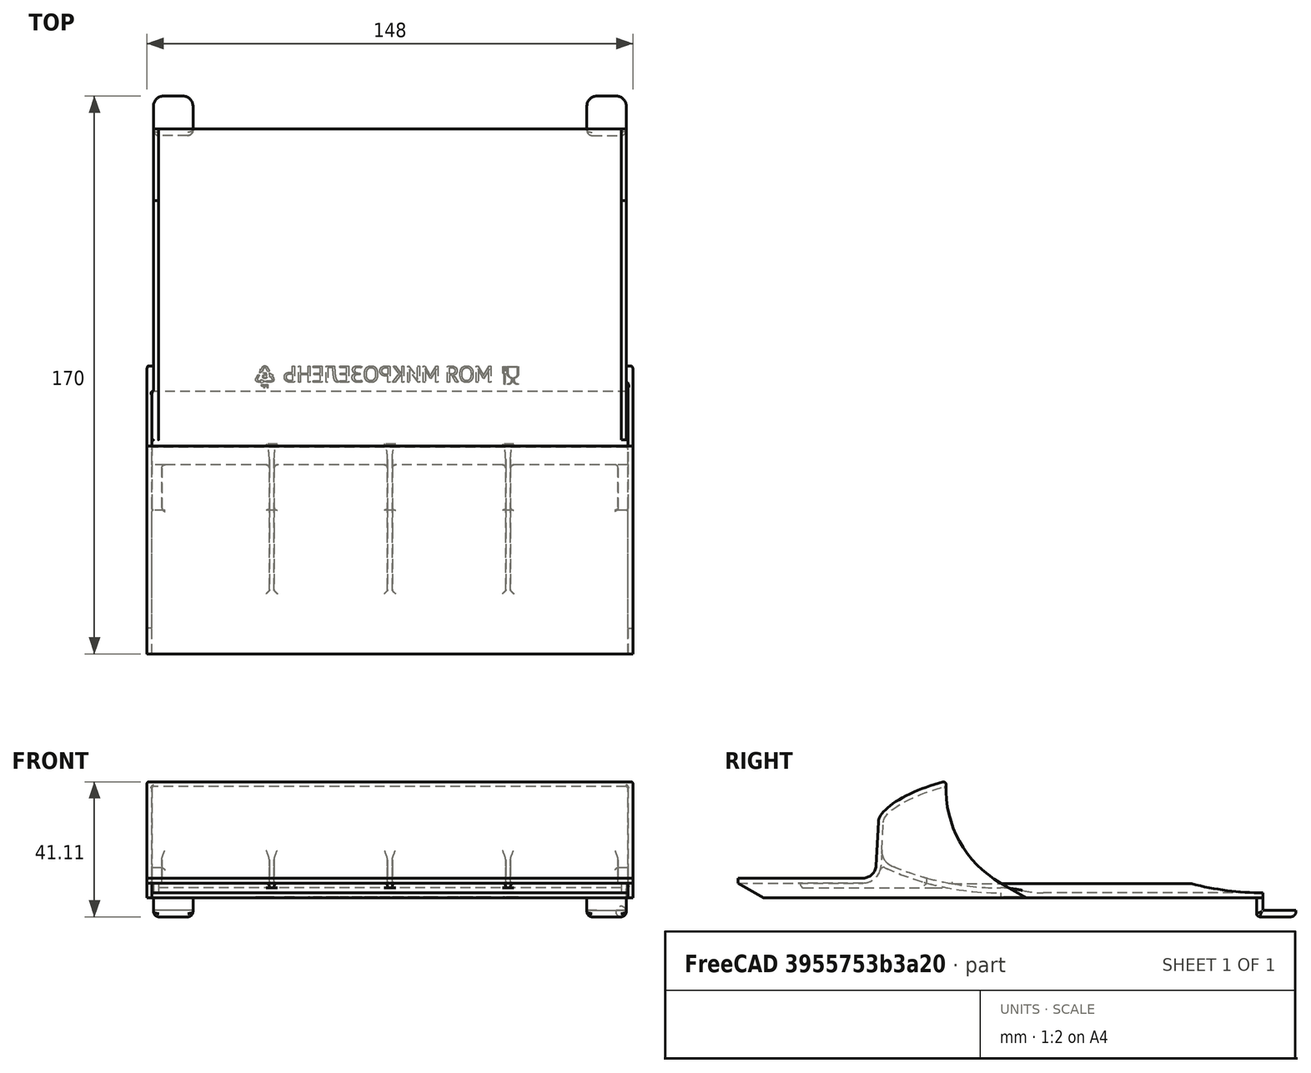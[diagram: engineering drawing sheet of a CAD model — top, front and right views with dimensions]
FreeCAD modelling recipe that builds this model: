
FCSTD DOCUMENT  (FreeCAD 1.1R38827 (Git))
Label: module
License: All rights reserved
LicenseURL: http://en.wikipedia.org/wiki/All_rights_reserved
objects: Sketcher::SketchObject×2, Part::Feature×1, PartDesign::FeatureBase×1, PartDesign::Body×1, Spreadsheet::Sheet×1
note: 8 computed .brp shape members not serialized (recipe doc carries the construction recipe); baked Part::Feature solids carry a one-line shape summary decoded from their .brp

FEATURE [Part::Feature] Part__Feature  label="module002"
  shape: bbox 170 x 148 x 41.12 mm, 715 faces (baked)
FEATURE [Sketcher::SketchObject] Sketch  label="module_holes"
  ArcFitTolerance = 0
  FullyConstrained = true
  MakeInternals = false
  sketch-geometry (10):
    g0: LineSegment StartX=59.5 StartY=-3.5 StartZ=0 EndX=59.5 EndY=3.5 EndZ=0
    g1: LineSegment StartX=59.5 StartY=3.5 StartZ=0 EndX=72.5 EndY=3.5 EndZ=0
    g2: LineSegment StartX=72.5 StartY=3.5 StartZ=0 EndX=72.5 EndY=-3.5 EndZ=0
    g3: LineSegment StartX=72.5 StartY=-3.5 StartZ=0 EndX=59.5 EndY=-3.5 EndZ=0
    g4: GeomPoint [constr] X=66 Y=0 Z=0
    g5: LineSegment StartX=-72.5 StartY=-3.5 StartZ=0 EndX=-72.5 EndY=3.5 EndZ=0
    g6: LineSegment StartX=-72.5 StartY=3.5 StartZ=0 EndX=-59.5 EndY=3.5 EndZ=0
    g7: LineSegment StartX=-59.5 StartY=3.5 StartZ=0 EndX=-59.5 EndY=-3.5 EndZ=0
    g8: LineSegment StartX=-59.5 StartY=-3.5 StartZ=0 EndX=-72.5 EndY=-3.5 EndZ=0
    g9: GeomPoint [constr] X=-66 Y=0 Z=0
  constraints (25):
    c: Coincident(g0,g1)
    c: Coincident(g1,g2)
    c: Coincident(g2,g3)
    c: Coincident(g3,g0)
    c: Horizontal(g1)
    c: Horizontal(g3)
    c: Vertical(g0)
    c: Vertical(g2)
    c: Symmetric(g1,g0,g4)
    c: PointOnObject(g4,g-1)
    c: Coincident(g5,g6)
    c: Coincident(g6,g7)
    c: Coincident(g7,g8)
    c: Coincident(g8,g5)
    c: Horizontal(g6)
    c: Horizontal(g8)
    c: Vertical(g5)
    c: Vertical(g7)
    c: Symmetric(g6,g5,g9)
    c: Symmetric(g9,g4,g-2)
    c: Equal(g1,g6)
    c: Equal(g7,g2)
    c: DistanceX(g1,g1) = 13
    c: DistanceY(g2,g2) = 7
    c: DistanceX(g9,g4) = 132
FEATURE [PartDesign::FeatureBase] BaseFeature
  BaseFeature = -> Part__Feature
  Placement = pos=(0,0,0) rot=(0,0,1;1.5708rad)
  Suppressed = false
FEATURE [PartDesign::Body] Body  label="module_Body"
  AllowCompound = false
  BaseFeature = -> Part__Feature
  Group = -> [BaseFeature]
  Origin = -> Origin
  Tip = -> BaseFeature
FEATURE [Spreadsheet::Sheet] Spreadsheet  label="Properties"
  cells = B2(module_width)==148 mm; C2(module_height)==160 mm; D2(module_fixture_distance_x)==132 mm; E2(module_fixture_distance_y)==80 mm; F2(module_hole_x)==13 mm; G2(module_hole_y)==7 mm
FEATURE [Sketcher::SketchObject] Sketch001  label="module_holes001"
  ArcFitTolerance = 0
  FullyConstrained = true
  MakeInternals = false
  sketch-geometry (10):
    g0: LineSegment StartX=59 StartY=-3.5 StartZ=0 EndX=59 EndY=3.5 EndZ=0
    g1: LineSegment StartX=59 StartY=3.5 StartZ=0 EndX=73 EndY=3.5 EndZ=0
    g2: LineSegment StartX=73 StartY=3.5 StartZ=0 EndX=73 EndY=-3.5 EndZ=0
    g3: LineSegment StartX=73 StartY=-3.5 StartZ=0 EndX=59 EndY=-3.5 EndZ=0
    g4: GeomPoint [constr] X=66 Y=0 Z=0
    g5: LineSegment StartX=-73 StartY=-3.5 StartZ=0 EndX=-73 EndY=3.5 EndZ=0
    g6: LineSegment StartX=-73 StartY=3.5 StartZ=0 EndX=-59 EndY=3.5 EndZ=0
    g7: LineSegment StartX=-59 StartY=3.5 StartZ=0 EndX=-59 EndY=-3.5 EndZ=0
    g8: LineSegment StartX=-59 StartY=-3.5 StartZ=0 EndX=-73 EndY=-3.5 EndZ=0
    g9: GeomPoint [constr] X=-66 Y=0 Z=0
  constraints (25):
    c: Coincident(g0,g1)
    c: Coincident(g1,g2)
    c: Coincident(g2,g3)
    c: Coincident(g3,g0)
    c: Horizontal(g1)
    c: Horizontal(g3)
    c: Vertical(g0)
    c: Vertical(g2)
    c: Symmetric(g1,g0,g4)
    c: PointOnObject(g4,g-1)
    c: Coincident(g5,g6)
    c: Coincident(g6,g7)
    c: Coincident(g7,g8)
    c: Coincident(g8,g5)
    c: Horizontal(g6)
    c: Horizontal(g8)
    c: Vertical(g5)
    c: Vertical(g7)
    c: Symmetric(g6,g5,g9)
    c: Symmetric(g9,g4,g-2)
    c: Equal(g1,g6)
    c: Equal(g7,g2)
    c: DistanceX(g1,g1) = 14
    c: DistanceY(g2,g2) = 7
    c: DistanceX(g9,g4) = 132
